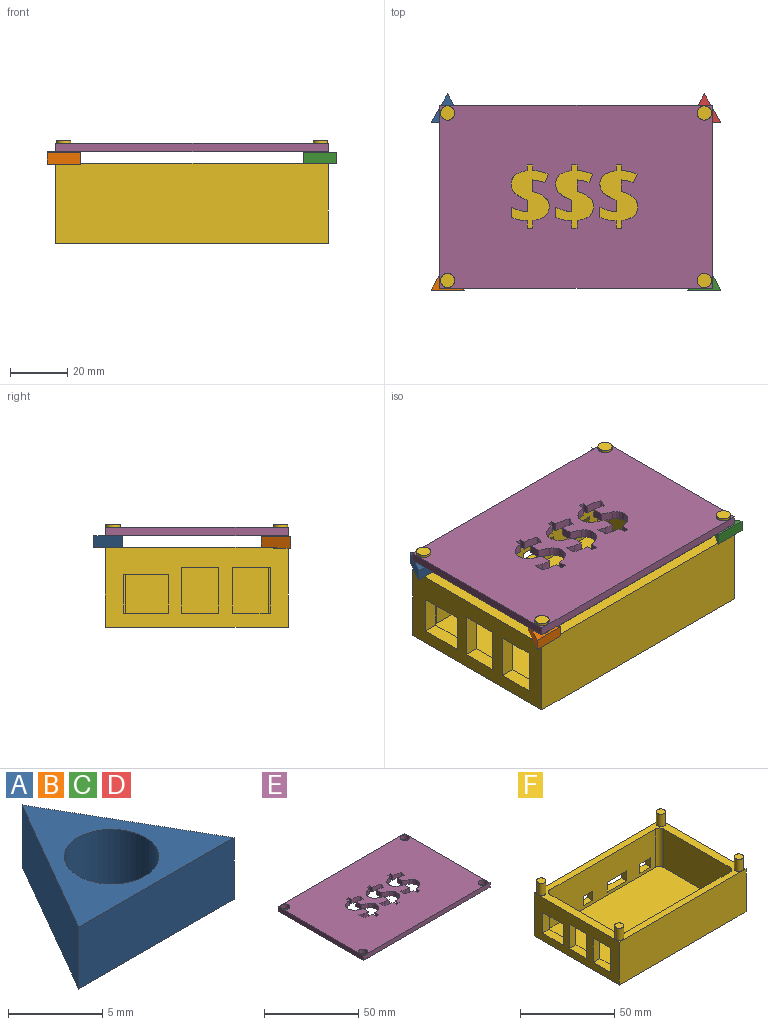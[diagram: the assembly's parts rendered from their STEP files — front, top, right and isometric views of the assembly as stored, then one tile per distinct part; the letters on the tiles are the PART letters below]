
ASSEMBLY  parts=6 mates=5
PART A: 6 faces, bbox 11.6x10.1x4 mm
  f0: plane 11.62x4mm, normal (0,-1,0), area 46.5mm2, adj f1,f3,f4,f5
  f1: plane 10.06x5.81mm, normal (0.87,0.5,0), area 46.5mm2, adj f0,f3,f4,f5
  f2: cylinder r=2.5mm len=5mm, axis (0,0,-1), area 62.8mm2, adj f4,f5
  f3: plane 10.06x5.81mm, normal (-0.87,0.5,0), area 46.5mm2, adj f0,f1,f4,f5
  f4: plane 11.62x10.06mm, normal (0,0,1), area 38.8mm2, adj f0,f1,f2,f3
  f5: plane 11.62x10.06mm, normal (0,0,-1), area 38.8mm2, adj f0,f1,f2,f3
PART B: same geometry as A
PART C: same geometry as A
PART D: same geometry as A
PART E: 85 faces, bbox 95.4x64.1x3 mm
  f0: plane 95.36x64.09mm, normal (0,0,1), area 5537.6mm2, adj f2,f3,f4,f5,f6,f7,f8,f9
  f1: plane 95.36x64.09mm, normal (0,0,-1), area 5537.6mm2, adj f2,f3,f4,f5,f6,f7,f8,f9
  f2: plane 95.36x3mm, normal (0,1,0), area 286.1mm2, adj f0,f1,f3,f5
  f3: plane 64.09x3mm, normal (-1,0,0), area 192.3mm2, adj f0,f1,f2,f4
  f4: plane 95.36x3mm, normal (0,-1,0), area 286.1mm2, adj f0,f1,f3,f5
  f5: plane 64.09x3mm, normal (1,0,0), area 192.3mm2, adj f0,f1,f2,f4
  f6: cylinder r=2.5mm len=5mm, axis (0,0,1), area 47.1mm2, adj f0,f1
  f7: cylinder r=2.5mm len=5mm, axis (0,0,1), area 47.1mm2, adj f0,f1
  f8: cylinder r=2.5mm len=5mm, axis (0,0,1), area 47.1mm2, adj f0,f1
  f9: cylinder r=2.5mm len=5mm, axis (0,0,1), area 47.1mm2, adj f0,f1
  f10: extruded ~4.28x3mm, area 13.8mm2, adj f0,f1,f11,f34
  f11: plane 3x2.72mm, normal (-1,0,0), area 8.2mm2, adj f0,f1,f10,f12
  f12: plane 3x1.82mm, normal (0,1,0), area 5.5mm2, adj f0,f1,f11,f13
  f13: plane 3x2.67mm, normal (1,0,0), area 8mm2, adj f0,f1,f12,f14
  f14: extruded ~5.69x3mm, area 17.5mm2, adj f0,f1,f13,f15
  f15: plane 3.51x3mm, normal (1,0,0), area 10.5mm2, adj f0,f1,f14,f16
  f16: extruded ~3x2.78mm, area 8.9mm2, adj f0,f1,f15,f17
  f17: extruded ~3x2.9mm, area 8.9mm2, adj f0,f1,f16,f18
  f18: plane 4.11x3mm, normal (1,0,0), area 12.3mm2, adj f0,f1,f17,f19
  f19: plane 3x0.89mm, normal (0.36,0.93,0), area 2.9mm2, adj f0,f1,f18,f20
  f20: extruded ~3.72x3mm, area 13.2mm2, adj f0,f1,f19,f21
  f21: extruded ~3.01x3mm, area 9.8mm2, adj f0,f1,f20,f22
  f22: extruded ~3.17x3mm, area 10.9mm2, adj f0,f1,f21,f23
  f23: extruded ~4.21x3mm, area 13.6mm2, adj f0,f1,f22,f24
  f24: plane 3x2.03mm, normal (1,0,0), area 6.1mm2, adj f0,f1,f23,f25
  f25: plane 3x1.82mm, normal (0,-1,0), area 5.5mm2, adj f0,f1,f24,f26
  f26: plane 3x1.98mm, normal (-1,0,0), area 5.9mm2, adj f0,f1,f25,f27
  f27: extruded ~5.5x3mm, area 17mm2, adj f0,f1,f26,f28
  f28: plane 3.11x3mm, normal (-0.93,0.37,0), area 10mm2, adj f0,f1,f27,f29
  f29: extruded ~4.25x3mm, area 13.2mm2, adj f0,f1,f28,f30
  f30: plane 3.92x3mm, normal (-1,0,0), area 11.8mm2, adj f0,f1,f29,f31
  f31: extruded ~3.68x3mm, area 12.2mm2, adj f0,f1,f30,f32
  f32: extruded ~3x1.61mm, area 6.9mm2, adj f0,f1,f31,f33
  f33: extruded ~3x2.05mm, area 6.4mm2, adj f0,f1,f32,f34
  f34: extruded ~3.39x3mm, area 11.6mm2, adj f0,f1,f10,f33
  f35: extruded ~4.28x3mm, area 13.8mm2, adj f0,f1,f36,f59
  f36: plane 3x2.72mm, normal (-1,0,0), area 8.2mm2, adj f0,f1,f35,f37
  f37: plane 3x1.82mm, normal (0,1,0), area 5.5mm2, adj f0,f1,f36,f38
  f38: plane 3x2.67mm, normal (1,0,0), area 8mm2, adj f0,f1,f37,f39
  f39: extruded ~5.69x3mm, area 17.5mm2, adj f0,f1,f38,f40
  f40: plane 3.51x3mm, normal (1,0,0), area 10.5mm2, adj f0,f1,f39,f41
  f41: extruded ~3x2.78mm, area 8.9mm2, adj f0,f1,f40,f42
  f42: extruded ~3x2.9mm, area 8.9mm2, adj f0,f1,f41,f43
  f43: plane 4.11x3mm, normal (1,0,0), area 12.3mm2, adj f0,f1,f42,f44
  f44: plane 3x0.89mm, normal (0.36,0.93,0), area 2.9mm2, adj f0,f1,f43,f45
  f45: extruded ~3.72x3mm, area 13.2mm2, adj f0,f1,f44,f46
  f46: extruded ~3.01x3mm, area 9.8mm2, adj f0,f1,f45,f47
  f47: extruded ~3.17x3mm, area 10.9mm2, adj f0,f1,f46,f48
  f48: extruded ~4.21x3mm, area 13.6mm2, adj f0,f1,f47,f49
  f49: plane 3x2.03mm, normal (1,0,0), area 6.1mm2, adj f0,f1,f48,f50
  f50: plane 3x1.82mm, normal (0,-1,0), area 5.5mm2, adj f0,f1,f49,f51
  f51: plane 3x1.98mm, normal (-1,0,0), area 5.9mm2, adj f0,f1,f50,f52
  f52: extruded ~5.5x3mm, area 17mm2, adj f0,f1,f51,f53
  f53: plane 3.11x3mm, normal (-0.93,0.37,0), area 10mm2, adj f0,f1,f52,f54
  f54: extruded ~4.25x3mm, area 13.2mm2, adj f0,f1,f53,f55
  f55: plane 3.92x3mm, normal (-1,0,0), area 11.8mm2, adj f0,f1,f54,f56
  f56: extruded ~3.68x3mm, area 12.2mm2, adj f0,f1,f55,f57
  f57: extruded ~3x1.61mm, area 6.9mm2, adj f0,f1,f56,f58
  f58: extruded ~3x2.05mm, area 6.4mm2, adj f0,f1,f57,f59
  f59: extruded ~3.39x3mm, area 11.6mm2, adj f0,f1,f35,f58
  f60: extruded ~4.28x3mm, area 13.8mm2, adj f0,f1,f61,f84
  f61: plane 3x2.72mm, normal (-1,0,0), area 8.2mm2, adj f0,f1,f60,f62
  f62: plane 3x1.82mm, normal (0,1,0), area 5.5mm2, adj f0,f1,f61,f63
  f63: plane 3x2.67mm, normal (1,0,0), area 8mm2, adj f0,f1,f62,f64
  f64: extruded ~5.69x3mm, area 17.5mm2, adj f0,f1,f63,f65
  f65: plane 3.51x3mm, normal (1,0,0), area 10.5mm2, adj f0,f1,f64,f66
  f66: extruded ~3x2.78mm, area 8.9mm2, adj f0,f1,f65,f67
  f67: extruded ~3x2.9mm, area 8.9mm2, adj f0,f1,f66,f68
  f68: plane 4.11x3mm, normal (1,0,0), area 12.3mm2, adj f0,f1,f67,f69
  f69: plane 3x0.89mm, normal (0.36,0.93,0), area 2.9mm2, adj f0,f1,f68,f70
  f70: extruded ~3.72x3mm, area 13.2mm2, adj f0,f1,f69,f71
  f71: extruded ~3.01x3mm, area 9.8mm2, adj f0,f1,f70,f72
  f72: extruded ~3.17x3mm, area 10.9mm2, adj f0,f1,f71,f73
  f73: extruded ~4.21x3mm, area 13.6mm2, adj f0,f1,f72,f74
  f74: plane 3x2.03mm, normal (1,0,0), area 6.1mm2, adj f0,f1,f73,f75
  f75: plane 3x1.82mm, normal (0,-1,0), area 5.5mm2, adj f0,f1,f74,f76
  f76: plane 3x1.98mm, normal (-1,0,0), area 5.9mm2, adj f0,f1,f75,f77
  f77: extruded ~5.5x3mm, area 17mm2, adj f0,f1,f76,f78
  f78: plane 3.11x3mm, normal (-0.93,0.37,0), area 10mm2, adj f0,f1,f77,f79
  f79: extruded ~4.25x3mm, area 13.2mm2, adj f0,f1,f78,f80
  f80: plane 3.92x3mm, normal (-1,0,0), area 11.8mm2, adj f0,f1,f79,f81
  f81: extruded ~3.68x3mm, area 12.2mm2, adj f0,f1,f80,f82
  f82: extruded ~3x1.61mm, area 6.9mm2, adj f0,f1,f81,f83
  f83: extruded ~3x2.05mm, area 6.4mm2, adj f0,f1,f82,f84
  f84: extruded ~3.39x3mm, area 11.6mm2, adj f0,f1,f60,f83
PART F: 47 faces, bbox 95.4x64.1x36 mm
  f0: plane 95.36x28mm, normal (0,1,0), area 2484.3mm2, adj f3,f11,f12,f25,f26,f27,f28,f29
  f1: plane 79.36x25mm, normal (0,-1,0), area 1798.3mm2, adj f4,f10,f12,f25,f26,f27,f28,f29
  f2: plane 95.36x28mm, normal (0,-1,0), area 2670mm2, adj f3,f11,f12,f38
  f3: plane 64.09x28mm, normal (1,0,0), area 1794.5mm2, adj f0,f2,f12,f38
  f4: cylinder r=3mm len=25mm, axis (0,0,-1), area 117.8mm2, adj f1,f5,f12,f37
  f5: plane 50.09x25mm, normal (-1,0,0), area 1252.2mm2, adj f4,f6,f12,f37
  f6: cylinder r=3mm len=25mm, axis (0,0,-1), area 117.8mm2, adj f5,f7,f12,f37
  f7: plane 79.36x25mm, normal (0,1,0), area 1984mm2, adj f6,f8,f12,f37
  f8: cylinder r=3mm len=25mm, axis (0,0,-1), area 106.6mm2, adj f7,f9,f12,f14,f15,f16,f37
  f9: plane 50.09x25mm, normal (1,0,0), area 636mm2, adj f8,f10,f12,f13,f14,f15,f17,f18
  f10: cylinder r=3mm len=25mm, axis (0,0,-1), area 110.4mm2, adj f1,f9,f12,f21,f22,f24,f37
  f11: plane 64.09x28mm, normal (-1,0,0), area 1159.9mm2, adj f0,f2,f12,f13,f14,f15,f16,f17
  f12: plane 95.36x64.09mm, normal (0,0,1), area 1253mm2, adj f0,f1,f2,f3,f4,f5,f6,f7
  f13: plane 16x5mm, normal (0,-1,0), area 80mm2, adj f9,f11,f14,f15
  f14: plane 13.3x5.08mm, normal (0,0,-1), area 66.5mm2, adj f8,f9,f11,f13,f16
  f15: plane 13.3x5.08mm, normal (0,0,1), area 66.5mm2, adj f8,f9,f11,f13,f16
  f16: plane 16x5.08mm, normal (0,1,0), area 81.3mm2, adj f8,f11,f14,f15
  f17: plane 13.07x5mm, normal (0,0,-1), area 65.3mm2, adj f9,f11,f18,f20
  f18: plane 16x5mm, normal (0,-1,0), area 80mm2, adj f9,f11,f17,f19
  f19: plane 13.07x5mm, normal (0,0,1), area 65.3mm2, adj f9,f11,f18,f20
  f20: plane 16x5mm, normal (0,1,0), area 80mm2, adj f9,f11,f17,f19
  f21: plane 15.76x5.05mm, normal (0,0,-1), area 78.8mm2, adj f9,f10,f11,f23,f24
  f22: plane 15.76x5.05mm, normal (0,0,1), area 78.8mm2, adj f9,f10,f11,f23,f24
  f23: plane 13.5x5mm, normal (0,1,0), area 67.5mm2, adj f9,f11,f21,f22
  f24: plane 13.5x5.05mm, normal (0,-1,0), area 68.2mm2, adj f10,f11,f21,f22
  f25: plane 6.5x4mm, normal (-1,0,0), area 26mm2, adj f0,f1,f26,f28
  f26: plane 14.6x4mm, normal (0,0,1), area 58.4mm2, adj f0,f1,f25,f27
  f27: plane 6.5x4mm, normal (1,0,0), area 26mm2, adj f0,f1,f26,f28
  f28: plane 14.6x4mm, normal (0,0,-1), area 58.4mm2, adj f0,f1,f25,f27
  f29: plane 7.14x4mm, normal (0,0,1), area 28.6mm2, adj f0,f1,f30,f32
  f30: plane 6x4mm, normal (1,0,0), area 24mm2, adj f0,f1,f29,f31
  f31: plane 7.14x4mm, normal (0,0,-1), area 28.6mm2, adj f0,f1,f30,f32
  f32: plane 6x4mm, normal (-1,0,0), area 24mm2, adj f0,f1,f29,f31
  f33: plane 6x4mm, normal (-1,0,0), area 24mm2, adj f0,f1,f34,f36
  f34: plane 7.99x4mm, normal (0,0,1), area 32mm2, adj f0,f1,f33,f35
  f35: plane 6x4mm, normal (1,0,0), area 24mm2, adj f0,f1,f34,f36
  f36: plane 7.99x4mm, normal (0,0,-1), area 32mm2, adj f0,f1,f33,f35
  f37: plane 85.36x56.09mm, normal (0,0,1), area 4780mm2, adj f1,f4,f5,f6,f7,f8,f9,f10
  f38: plane 95.36x64.09mm, normal (0,0,-1), area 6111.5mm2, adj f0,f2,f3,f11
  f39: cylinder r=2.5mm len=8mm, axis (0,0,-1), area 125.7mm2, adj f12,f40
  f40: plane 5x5mm, normal (0,0,1), area 19.6mm2, adj f39
  f41: cylinder r=2.5mm len=8mm, axis (0,0,-1), area 125.7mm2, adj f12,f42
  f42: plane 5x5mm, normal (0,0,1), area 19.6mm2, adj f41
  f43: cylinder r=2.5mm len=8mm, axis (0,0,-1), area 125.7mm2, adj f12,f44
  f44: plane 5x5mm, normal (0,0,1), area 19.6mm2, adj f43
  f45: cylinder r=2.5mm len=8mm, axis (0,0,-1), area 125.7mm2, adj f12,f46
  f46: plane 5x5mm, normal (0,0,1), area 19.6mm2, adj f45
PLACE A t=(-146.26,20.46,69.03)mm
PLACE B rot(axis=(0,0,1),0deg) t=(-146.26,-38.19,68.65)mm
PLACE C rot(axis=(0,0,-1),0deg) t=(-56.34,-38.19,68.89)mm
PLACE D rot(axis=(0,0,1),0deg) t=(-56.34,20.46,68.88)mm
PLACE E t=(-101.51,-8.89,73.03)mm
PLACE F rot(axis=(0,0,-1),0deg) t=(-101.96,-8.28,43.91)mm
MATE cylindrical F.f43 <-> C.f2  axis (0,0,-1) through (-56.34,-38.19,72.91)mm
MATE cylindrical F.f41 <-> D.f2  axis (0,0,-1) through (-56.34,20.46,72.91)mm
MATE cylindrical E.f7 <-> F.f43  axis (0,0,1) through (-56.34,-38.19,76.03)mm
MATE cylindrical F.f39 <-> A.f2  axis (0,0,-1) through (-146.26,20.46,72.91)mm
MATE cylindrical F.f45 <-> B.f2  axis (0,0,-1) through (-146.26,-38.19,72.91)mm
